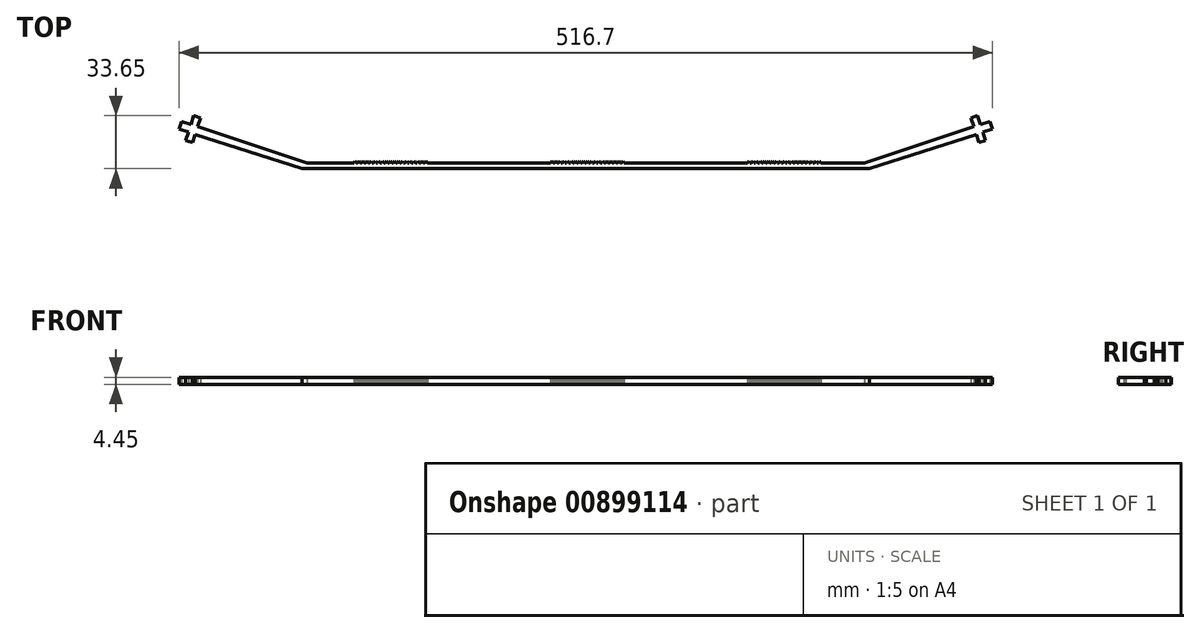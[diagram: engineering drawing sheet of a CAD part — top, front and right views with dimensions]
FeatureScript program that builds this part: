
annotation { "Feature Type Name" : "Feature", "Feature Type Description" : "" }
export const myFeature = defineFeature(function(context is Context, id is Id, definition is map)
    precondition{}
    {
        {
            var Q0;
            Q0=qCreatedBy(makeId("Top.planeOp"),FACE);
            var sketch = newSketch(context, id + "F0", { "sketchPlane" : qUnion([Q0])});
            skLineSegment(sketch, "E0", {"start": v(-260.7, 10.38) * mm, "end": v(94.9, 10.38) * mm});
            skLineSegment(sketch, "E1", {"start": v(-259.95, 14.04) * mm, "end": v(-232.45, 14.04) * mm});
            skLineSegment(sketch, "E2", {"start": v(-84.08, 15.18) * mm, "end": v(-83.22, 14.04) * mm});
            skLineSegment(sketch, "E3.MirrorCS", {"start": v(-84.08, 15.18) * mm, "end": v(-84.95, 14.04) * mm});
            skLineSegment(sketch, "E4.trimOffspring", {"start": v(-83.22, 14.04) * mm, "end": v(-82.45, 14.04) * mm});
            skPoint(sketch, "E5.start.orphan", {"position": v(-84.08, 8) * mm});
            skLineSegment(sketch, "E6.direction1", {"start": v(-83.22, 14.04) * mm, "end": v(-82.45, 14.04) * mm, "construction": true});
            skLineSegment(sketch, "E7.1.0.0", {"start": v(-81.58, 15.18) * mm, "end": v(-80.72, 14.04) * mm});
            skLineSegment(sketch, "E7.1.0.1", {"start": v(-81.58, 15.18) * mm, "end": v(-82.45, 14.04) * mm});
            skLineSegment(sketch, "E7.2.0.0", {"start": v(-79.08, 15.18) * mm, "end": v(-78.22, 14.04) * mm});
            skLineSegment(sketch, "E7.2.0.1", {"start": v(-79.08, 15.18) * mm, "end": v(-79.95, 14.04) * mm});
            skLineSegment(sketch, "E7.3.0.0", {"start": v(-76.58, 15.18) * mm, "end": v(-75.72, 14.04) * mm});
            skLineSegment(sketch, "E7.3.0.1", {"start": v(-76.58, 15.18) * mm, "end": v(-77.45, 14.04) * mm});
            skLineSegment(sketch, "E7.4.0.0", {"start": v(-74.08, 15.18) * mm, "end": v(-73.22, 14.04) * mm});
            skLineSegment(sketch, "E7.4.0.1", {"start": v(-74.08, 15.18) * mm, "end": v(-74.95, 14.04) * mm});
            skLineSegment(sketch, "E7.5.0.0", {"start": v(-71.58, 15.18) * mm, "end": v(-70.72, 14.04) * mm});
            skLineSegment(sketch, "E7.5.0.1", {"start": v(-71.58, 15.18) * mm, "end": v(-72.45, 14.04) * mm});
            skLineSegment(sketch, "E7.6.0.0", {"start": v(-69.08, 15.18) * mm, "end": v(-68.22, 14.04) * mm});
            skLineSegment(sketch, "E7.6.0.1", {"start": v(-69.08, 15.18) * mm, "end": v(-69.95, 14.04) * mm});
            skLineSegment(sketch, "E7.7.0.0", {"start": v(-66.58, 15.18) * mm, "end": v(-65.72, 14.04) * mm});
            skLineSegment(sketch, "E7.7.0.1", {"start": v(-66.58, 15.18) * mm, "end": v(-67.45, 14.04) * mm});
            skLineSegment(sketch, "E7.8.0.0", {"start": v(-64.08, 15.18) * mm, "end": v(-63.22, 14.04) * mm});
            skLineSegment(sketch, "E7.8.0.1", {"start": v(-64.08, 15.18) * mm, "end": v(-64.95, 14.04) * mm});
            skLineSegment(sketch, "E7.9.0.0", {"start": v(-61.58, 15.18) * mm, "end": v(-60.72, 14.04) * mm});
            skLineSegment(sketch, "E7.9.0.1", {"start": v(-61.58, 15.18) * mm, "end": v(-62.45, 14.04) * mm});
            skLineSegment(sketch, "E8.1.0.0", {"start": v(-86.58, 15.18) * mm, "end": v(-87.45, 14.04) * mm});
            skLineSegment(sketch, "E8.1.0.1", {"start": v(-86.58, 15.18) * mm, "end": v(-85.72, 14.04) * mm});
            skLineSegment(sketch, "E8.2.0.0", {"start": v(-89.08, 15.18) * mm, "end": v(-89.95, 14.04) * mm});
            skLineSegment(sketch, "E8.2.0.1", {"start": v(-89.08, 15.18) * mm, "end": v(-88.22, 14.04) * mm});
            skLineSegment(sketch, "E8.3.0.0", {"start": v(-91.58, 15.18) * mm, "end": v(-92.45, 14.04) * mm});
            skLineSegment(sketch, "E8.3.0.1", {"start": v(-91.58, 15.18) * mm, "end": v(-90.72, 14.04) * mm});
            skLineSegment(sketch, "E8.4.0.0", {"start": v(-94.08, 15.18) * mm, "end": v(-94.95, 14.04) * mm});
            skLineSegment(sketch, "E8.4.0.1", {"start": v(-94.08, 15.18) * mm, "end": v(-93.22, 14.04) * mm});
            skLineSegment(sketch, "E8.5.0.0", {"start": v(-96.58, 15.18) * mm, "end": v(-97.45, 14.04) * mm});
            skLineSegment(sketch, "E8.5.0.1", {"start": v(-96.58, 15.18) * mm, "end": v(-95.72, 14.04) * mm});
            skLineSegment(sketch, "E8.6.0.0", {"start": v(-99.08, 15.18) * mm, "end": v(-99.95, 14.04) * mm});
            skLineSegment(sketch, "E8.6.0.1", {"start": v(-99.08, 15.18) * mm, "end": v(-98.22, 14.04) * mm});
            skLineSegment(sketch, "E8.7.0.0", {"start": v(-101.58, 15.18) * mm, "end": v(-102.45, 14.04) * mm});
            skLineSegment(sketch, "E8.7.0.1", {"start": v(-101.58, 15.18) * mm, "end": v(-100.72, 14.04) * mm});
            skLineSegment(sketch, "E8.8.0.0", {"start": v(-104.08, 15.18) * mm, "end": v(-104.95, 14.04) * mm});
            skLineSegment(sketch, "E8.8.0.1", {"start": v(-104.08, 15.18) * mm, "end": v(-103.22, 14.04) * mm});
            skLineSegment(sketch, "E8.9.0.0", {"start": v(-106.58, 15.18) * mm, "end": v(-107.45, 14.04) * mm});
            skLineSegment(sketch, "E8.9.0.1", {"start": v(-106.58, 15.18) * mm, "end": v(-105.72, 14.04) * mm});
            skLineSegment(sketch, "E8.direction1", {"start": v(-84.95, 14.04) * mm, "end": v(-85.72, 14.04) * mm, "construction": true});
            skLineSegment(sketch, "E9.trimOffspring", {"start": v(-105.72, 14.04) * mm, "end": v(-104.95, 14.04) * mm});
            skLineSegment(sketch, "E10.trimOffspring", {"start": v(-103.22, 14.04) * mm, "end": v(-102.45, 14.04) * mm});
            skLineSegment(sketch, "E11.trimOffspring", {"start": v(-100.72, 14.04) * mm, "end": v(-99.95, 14.04) * mm});
            skLineSegment(sketch, "E12.trimOffspring", {"start": v(-95.72, 14.04) * mm, "end": v(-94.95, 14.04) * mm});
            skLineSegment(sketch, "E13.trimOffspring", {"start": v(-98.22, 14.04) * mm, "end": v(-97.45, 14.04) * mm});
            skLineSegment(sketch, "E14.trimOffspring", {"start": v(-93.22, 14.04) * mm, "end": v(-92.45, 14.04) * mm});
            skLineSegment(sketch, "E15.trimOffspring", {"start": v(-90.72, 14.04) * mm, "end": v(-89.95, 14.04) * mm});
            skLineSegment(sketch, "E16.trimOffspring", {"start": v(-88.22, 14.04) * mm, "end": v(-87.45, 14.04) * mm});
            skLineSegment(sketch, "E17.trimOffspring", {"start": v(-85.72, 14.04) * mm, "end": v(-84.95, 14.04) * mm});
            skLineSegment(sketch, "E18.trimOffspring", {"start": v(-80.72, 14.04) * mm, "end": v(-79.95, 14.04) * mm, "construction": true});
            skLineSegment(sketch, "E19.trimOffspring", {"start": v(-80.72, 14.04) * mm, "end": v(-79.95, 14.04) * mm});
            skLineSegment(sketch, "E20.trimOffspring", {"start": v(-78.22, 14.04) * mm, "end": v(-77.45, 14.04) * mm, "construction": true});
            skLineSegment(sketch, "E21.trimOffspring", {"start": v(-78.22, 14.04) * mm, "end": v(-77.45, 14.04) * mm});
            skLineSegment(sketch, "E22.trimOffspring", {"start": v(-75.72, 14.04) * mm, "end": v(-74.95, 14.04) * mm, "construction": true});
            skLineSegment(sketch, "E23.trimOffspring", {"start": v(-73.22, 14.04) * mm, "end": v(-72.45, 14.04) * mm, "construction": true});
            skLineSegment(sketch, "E24.trimOffspring", {"start": v(-73.22, 14.04) * mm, "end": v(-72.45, 14.04) * mm});
            skLineSegment(sketch, "E25", {"start": v(-75.72, 14.04) * mm, "end": v(-74.95, 14.04) * mm});
            skLineSegment(sketch, "E26.trimOffspring", {"start": v(-70.72, 14.04) * mm, "end": v(-69.95, 14.04) * mm, "construction": true});
            skLineSegment(sketch, "E27.trimOffspring", {"start": v(-70.72, 14.04) * mm, "end": v(-69.95, 14.04) * mm});
            skLineSegment(sketch, "E28.trimOffspring", {"start": v(-68.22, 14.04) * mm, "end": v(-67.45, 14.04) * mm, "construction": true});
            skLineSegment(sketch, "E29.trimOffspring", {"start": v(-68.22, 14.04) * mm, "end": v(-67.45, 14.04) * mm});
            skLineSegment(sketch, "E30.trimOffspring", {"start": v(-65.72, 14.04) * mm, "end": v(-64.95, 14.04) * mm, "construction": true});
            skLineSegment(sketch, "E31.trimOffspring", {"start": v(-65.72, 14.04) * mm, "end": v(-64.95, 14.04) * mm});
            skLineSegment(sketch, "E32.trimOffspring", {"start": v(-63.22, 14.04) * mm, "end": v(-62.45, 14.04) * mm, "construction": true});
            skLineSegment(sketch, "E33.trimOffspring", {"start": v(-63.22, 14.04) * mm, "end": v(-62.45, 14.04) * mm});
            skLineSegment(sketch, "E34.trimOffspring", {"start": v(-60.72, 14.04) * mm, "end": v(-58.22, 14.04) * mm, "construction": true});
            skLineSegment(sketch, "E35.trimOffspring", {"start": v(-60.72, 14.04) * mm, "end": v(17.55, 14.04) * mm});
            skLineSegment(sketch, "E36.1.0.0", {"start": v(63.42, 15.18) * mm, "end": v(64.28, 14.04) * mm});
            skLineSegment(sketch, "E36.1.0.1", {"start": v(63.42, 15.18) * mm, "end": v(62.55, 14.04) * mm});
            skLineSegment(sketch, "E36.1.0.2", {"start": v(60.92, 15.18) * mm, "end": v(61.78, 14.04) * mm});
            skLineSegment(sketch, "E36.1.0.3", {"start": v(60.92, 15.18) * mm, "end": v(60.05, 14.04) * mm});
            skLineSegment(sketch, "E36.1.0.4", {"start": v(58.42, 15.18) * mm, "end": v(59.28, 14.04) * mm});
            skLineSegment(sketch, "E36.1.0.5", {"start": v(58.42, 15.18) * mm, "end": v(57.55, 14.04) * mm});
            skLineSegment(sketch, "E36.1.0.6", {"start": v(55.92, 15.18) * mm, "end": v(56.78, 14.04) * mm});
            skLineSegment(sketch, "E36.1.0.7", {"start": v(55.92, 15.18) * mm, "end": v(55.05, 14.04) * mm});
            skLineSegment(sketch, "E36.1.0.8", {"start": v(53.42, 15.18) * mm, "end": v(54.28, 14.04) * mm});
            skLineSegment(sketch, "E36.1.0.9", {"start": v(53.42, 15.18) * mm, "end": v(52.55, 14.04) * mm});
            skLineSegment(sketch, "E36.1.0.10", {"start": v(50.92, 15.18) * mm, "end": v(51.78, 14.04) * mm});
            skLineSegment(sketch, "E36.1.0.11", {"start": v(50.92, 15.18) * mm, "end": v(50.05, 14.04) * mm});
            skLineSegment(sketch, "E36.1.0.12", {"start": v(48.42, 15.18) * mm, "end": v(49.28, 14.04) * mm});
            skLineSegment(sketch, "E36.1.0.13", {"start": v(48.42, 15.18) * mm, "end": v(47.55, 14.04) * mm});
            skLineSegment(sketch, "E36.1.0.14", {"start": v(45.92, 15.18) * mm, "end": v(46.78, 14.04) * mm});
            skLineSegment(sketch, "E36.1.0.15", {"start": v(45.92, 15.18) * mm, "end": v(45.05, 14.04) * mm});
            skLineSegment(sketch, "E36.1.0.16", {"start": v(43.42, 15.18) * mm, "end": v(44.28, 14.04) * mm});
            skLineSegment(sketch, "E36.1.0.17", {"start": v(43.42, 15.18) * mm, "end": v(42.55, 14.04) * mm});
            skLineSegment(sketch, "E36.1.0.18", {"start": v(40.92, 15.18) * mm, "end": v(41.78, 14.04) * mm});
            skLineSegment(sketch, "E36.1.0.19", {"start": v(40.92, 15.18) * mm, "end": v(40.05, 14.04) * mm});
            skLineSegment(sketch, "E36.1.0.20", {"start": v(38.42, 15.18) * mm, "end": v(39.28, 14.04) * mm});
            skLineSegment(sketch, "E36.1.0.21", {"start": v(38.42, 15.18) * mm, "end": v(37.55, 14.04) * mm});
            skLineSegment(sketch, "E36.1.0.22", {"start": v(35.92, 15.18) * mm, "end": v(36.78, 14.04) * mm});
            skLineSegment(sketch, "E36.1.0.23", {"start": v(35.92, 15.18) * mm, "end": v(35.05, 14.04) * mm});
            skLineSegment(sketch, "E36.1.0.24", {"start": v(33.42, 15.18) * mm, "end": v(34.28, 14.04) * mm});
            skLineSegment(sketch, "E36.1.0.25", {"start": v(33.42, 15.18) * mm, "end": v(32.55, 14.04) * mm});
            skLineSegment(sketch, "E36.1.0.26", {"start": v(30.92, 15.18) * mm, "end": v(31.78, 14.04) * mm});
            skLineSegment(sketch, "E36.1.0.27", {"start": v(30.92, 15.18) * mm, "end": v(30.05, 14.04) * mm});
            skLineSegment(sketch, "E36.1.0.28", {"start": v(28.42, 15.18) * mm, "end": v(29.28, 14.04) * mm});
            skLineSegment(sketch, "E36.1.0.29", {"start": v(28.42, 15.18) * mm, "end": v(27.55, 14.04) * mm});
            skLineSegment(sketch, "E36.1.0.30", {"start": v(25.92, 15.18) * mm, "end": v(26.78, 14.04) * mm});
            skLineSegment(sketch, "E36.1.0.31", {"start": v(25.92, 15.18) * mm, "end": v(25.05, 14.04) * mm});
            skLineSegment(sketch, "E36.1.0.32", {"start": v(23.42, 15.18) * mm, "end": v(24.28, 14.04) * mm});
            skLineSegment(sketch, "E36.1.0.33", {"start": v(23.42, 15.18) * mm, "end": v(22.55, 14.04) * mm});
            skLineSegment(sketch, "E36.1.0.34", {"start": v(20.92, 15.18) * mm, "end": v(21.78, 14.04) * mm});
            skLineSegment(sketch, "E36.1.0.35", {"start": v(20.92, 15.18) * mm, "end": v(20.05, 14.04) * mm});
            skLineSegment(sketch, "E36.1.0.36", {"start": v(18.42, 15.18) * mm, "end": v(19.28, 14.04) * mm});
            skLineSegment(sketch, "E36.1.0.37", {"start": v(18.42, 15.18) * mm, "end": v(17.55, 14.04) * mm});
            skLineSegment(sketch, "E37.1.0.0", {"start": v(-186.58, 15.18) * mm, "end": v(-185.72, 14.04) * mm});
            skLineSegment(sketch, "E37.1.0.1", {"start": v(-186.58, 15.18) * mm, "end": v(-187.45, 14.04) * mm});
            skLineSegment(sketch, "E37.1.0.2", {"start": v(-189.08, 15.18) * mm, "end": v(-188.22, 14.04) * mm});
            skLineSegment(sketch, "E37.1.0.3", {"start": v(-189.08, 15.18) * mm, "end": v(-189.95, 14.04) * mm});
            skLineSegment(sketch, "E37.1.0.4", {"start": v(-191.58, 15.18) * mm, "end": v(-190.72, 14.04) * mm});
            skLineSegment(sketch, "E37.1.0.5", {"start": v(-191.58, 15.18) * mm, "end": v(-192.45, 14.04) * mm});
            skLineSegment(sketch, "E37.1.0.6", {"start": v(-194.08, 15.18) * mm, "end": v(-193.22, 14.04) * mm});
            skLineSegment(sketch, "E37.1.0.7", {"start": v(-194.08, 15.18) * mm, "end": v(-194.95, 14.04) * mm});
            skLineSegment(sketch, "E37.1.0.8", {"start": v(-196.58, 15.18) * mm, "end": v(-195.72, 14.04) * mm});
            skLineSegment(sketch, "E37.1.0.9", {"start": v(-196.58, 15.18) * mm, "end": v(-197.45, 14.04) * mm});
            skLineSegment(sketch, "E37.1.0.10", {"start": v(-199.08, 15.18) * mm, "end": v(-198.22, 14.04) * mm});
            skLineSegment(sketch, "E37.1.0.11", {"start": v(-199.08, 15.18) * mm, "end": v(-199.95, 14.04) * mm});
            skLineSegment(sketch, "E37.1.0.12", {"start": v(-201.58, 15.18) * mm, "end": v(-200.72, 14.04) * mm});
            skLineSegment(sketch, "E37.1.0.13", {"start": v(-201.58, 15.18) * mm, "end": v(-202.45, 14.04) * mm});
            skLineSegment(sketch, "E37.1.0.14", {"start": v(-204.08, 15.18) * mm, "end": v(-203.22, 14.04) * mm});
            skLineSegment(sketch, "E37.1.0.15", {"start": v(-204.08, 15.18) * mm, "end": v(-204.95, 14.04) * mm});
            skLineSegment(sketch, "E37.1.0.16", {"start": v(-206.58, 15.18) * mm, "end": v(-205.72, 14.04) * mm});
            skLineSegment(sketch, "E37.1.0.17", {"start": v(-206.58, 15.18) * mm, "end": v(-207.45, 14.04) * mm});
            skLineSegment(sketch, "E37.1.0.18", {"start": v(-209.08, 15.18) * mm, "end": v(-208.22, 14.04) * mm});
            skLineSegment(sketch, "E37.1.0.19", {"start": v(-209.08, 15.18) * mm, "end": v(-209.95, 14.04) * mm});
            skLineSegment(sketch, "E37.1.0.20", {"start": v(-231.58, 15.18) * mm, "end": v(-232.45, 14.04) * mm});
            skLineSegment(sketch, "E37.1.0.21", {"start": v(-231.58, 15.18) * mm, "end": v(-230.72, 14.04) * mm});
            skLineSegment(sketch, "E37.1.0.22", {"start": v(-229.08, 15.18) * mm, "end": v(-229.95, 14.04) * mm});
            skLineSegment(sketch, "E37.1.0.23", {"start": v(-229.08, 15.18) * mm, "end": v(-228.22, 14.04) * mm});
            skLineSegment(sketch, "E37.1.0.24", {"start": v(-226.58, 15.18) * mm, "end": v(-227.45, 14.04) * mm});
            skLineSegment(sketch, "E37.1.0.25", {"start": v(-226.58, 15.18) * mm, "end": v(-225.72, 14.04) * mm});
            skLineSegment(sketch, "E37.1.0.26", {"start": v(-224.08, 15.18) * mm, "end": v(-224.95, 14.04) * mm});
            skLineSegment(sketch, "E37.1.0.27", {"start": v(-224.08, 15.18) * mm, "end": v(-223.22, 14.04) * mm});
            skLineSegment(sketch, "E37.1.0.28", {"start": v(-221.58, 15.18) * mm, "end": v(-222.45, 14.04) * mm});
            skLineSegment(sketch, "E37.1.0.29", {"start": v(-221.58, 15.18) * mm, "end": v(-220.72, 14.04) * mm});
            skLineSegment(sketch, "E37.1.0.30", {"start": v(-219.08, 15.18) * mm, "end": v(-219.95, 14.04) * mm});
            skLineSegment(sketch, "E37.1.0.31", {"start": v(-219.08, 15.18) * mm, "end": v(-218.22, 14.04) * mm});
            skLineSegment(sketch, "E37.1.0.32", {"start": v(-216.58, 15.18) * mm, "end": v(-217.45, 14.04) * mm});
            skLineSegment(sketch, "E37.1.0.33", {"start": v(-216.58, 15.18) * mm, "end": v(-215.72, 14.04) * mm});
            skLineSegment(sketch, "E37.1.0.34", {"start": v(-214.08, 15.18) * mm, "end": v(-214.95, 14.04) * mm});
            skLineSegment(sketch, "E37.1.0.35", {"start": v(-214.08, 15.18) * mm, "end": v(-213.22, 14.04) * mm});
            skLineSegment(sketch, "E37.1.0.36", {"start": v(-211.58, 15.18) * mm, "end": v(-212.45, 14.04) * mm});
            skLineSegment(sketch, "E37.1.0.37", {"start": v(-211.58, 15.18) * mm, "end": v(-210.72, 14.04) * mm});
            skLineSegment(sketch, "E37.direction1", {"start": v(-60.72, 14.04) * mm, "end": v(-185.72, 14.04) * mm, "construction": true});
            skLineSegment(sketch, "E38.trimOffspring", {"start": v(-230.72, 14.04) * mm, "end": v(-229.95, 14.04) * mm});
            skLineSegment(sketch, "E39.trimOffspring", {"start": v(-228.22, 14.04) * mm, "end": v(-227.45, 14.04) * mm});
            skLineSegment(sketch, "E40.trimOffspring", {"start": v(-225.72, 14.04) * mm, "end": v(-224.95, 14.04) * mm});
            skLineSegment(sketch, "E41.trimOffspring", {"start": v(-223.22, 14.04) * mm, "end": v(-222.45, 14.04) * mm});
            skLineSegment(sketch, "E42.trimOffspring", {"start": v(-220.72, 14.04) * mm, "end": v(-219.95, 14.04) * mm});
            skLineSegment(sketch, "E43.trimOffspring", {"start": v(-218.22, 14.04) * mm, "end": v(-217.45, 14.04) * mm});
            skLineSegment(sketch, "E44.trimOffspring", {"start": v(-215.72, 14.04) * mm, "end": v(-214.95, 14.04) * mm});
            skLineSegment(sketch, "E45.trimOffspring", {"start": v(-213.22, 14.04) * mm, "end": v(-212.45, 14.04) * mm});
            skLineSegment(sketch, "E46.trimOffspring", {"start": v(-210.72, 14.04) * mm, "end": v(-209.95, 14.04) * mm});
            skLineSegment(sketch, "E47.trimOffspring", {"start": v(-208.22, 14.04) * mm, "end": v(-207.45, 14.04) * mm});
            skLineSegment(sketch, "E48.trimOffspring", {"start": v(-205.72, 14.04) * mm, "end": v(-204.95, 14.04) * mm});
            skLineSegment(sketch, "E49.trimOffspring", {"start": v(-203.22, 14.04) * mm, "end": v(-202.45, 14.04) * mm});
            skLineSegment(sketch, "E50.trimOffspring", {"start": v(-200.72, 14.04) * mm, "end": v(-199.95, 14.04) * mm});
            skLineSegment(sketch, "E51.trimOffspring", {"start": v(-198.22, 14.04) * mm, "end": v(-197.45, 14.04) * mm});
            skLineSegment(sketch, "E52.trimOffspring", {"start": v(-195.72, 14.04) * mm, "end": v(-194.95, 14.04) * mm});
            skLineSegment(sketch, "E53.trimOffspring", {"start": v(-193.22, 14.04) * mm, "end": v(-192.45, 14.04) * mm});
            skLineSegment(sketch, "E54.trimOffspring", {"start": v(-190.72, 14.04) * mm, "end": v(-189.95, 14.04) * mm});
            skLineSegment(sketch, "E55.trimOffspring", {"start": v(-188.22, 14.04) * mm, "end": v(-187.45, 14.04) * mm});
            skLineSegment(sketch, "E56.trimOffspring", {"start": v(-185.72, 14.04) * mm, "end": v(-107.45, 14.04) * mm});
            skLineSegment(sketch, "E57.trimOffspring", {"start": v(64.28, 14.04) * mm, "end": v(91.78, 14.04) * mm});
            skLineSegment(sketch, "E58.trimOffspring", {"start": v(61.78, 14.04) * mm, "end": v(62.55, 14.04) * mm, "construction": true});
            skLineSegment(sketch, "E59.trimOffspring", {"start": v(61.78, 14.04) * mm, "end": v(62.55, 14.04) * mm});
            skLineSegment(sketch, "E60.trimOffspring", {"start": v(59.28, 14.04) * mm, "end": v(60.05, 14.04) * mm, "construction": true});
            skLineSegment(sketch, "E61.trimOffspring", {"start": v(59.28, 14.04) * mm, "end": v(60.05, 14.04) * mm});
            skLineSegment(sketch, "E62.trimOffspring", {"start": v(56.78, 14.04) * mm, "end": v(57.55, 14.04) * mm, "construction": true});
            skLineSegment(sketch, "E63.trimOffspring", {"start": v(56.78, 14.04) * mm, "end": v(57.55, 14.04) * mm});
            skLineSegment(sketch, "E64.trimOffspring", {"start": v(54.28, 14.04) * mm, "end": v(55.05, 14.04) * mm, "construction": true});
            skLineSegment(sketch, "E65.trimOffspring", {"start": v(54.28, 14.04) * mm, "end": v(55.05, 14.04) * mm});
            skLineSegment(sketch, "E66.trimOffspring", {"start": v(51.78, 14.04) * mm, "end": v(52.55, 14.04) * mm});
            skLineSegment(sketch, "E67.trimOffspring", {"start": v(49.28, 14.04) * mm, "end": v(50.05, 14.04) * mm});
            skLineSegment(sketch, "E68.trimOffspring", {"start": v(46.78, 14.04) * mm, "end": v(47.55, 14.04) * mm});
            skLineSegment(sketch, "E69.trimOffspring", {"start": v(44.28, 14.04) * mm, "end": v(45.05, 14.04) * mm});
            skLineSegment(sketch, "E70.trimOffspring", {"start": v(41.78, 14.04) * mm, "end": v(42.55, 14.04) * mm});
            skLineSegment(sketch, "E71.trimOffspring", {"start": v(39.28, 14.04) * mm, "end": v(40.05, 14.04) * mm});
            skLineSegment(sketch, "E72.trimOffspring", {"start": v(36.78, 14.04) * mm, "end": v(37.55, 14.04) * mm});
            skLineSegment(sketch, "E73.trimOffspring", {"start": v(34.28, 14.04) * mm, "end": v(35.05, 14.04) * mm});
            skLineSegment(sketch, "E74.trimOffspring", {"start": v(19.28, 14.04) * mm, "end": v(20.05, 14.04) * mm});
            skLineSegment(sketch, "E75.trimOffspring", {"start": v(21.78, 14.04) * mm, "end": v(22.55, 14.04) * mm});
            skLineSegment(sketch, "E76.trimOffspring", {"start": v(24.28, 14.04) * mm, "end": v(25.05, 14.04) * mm});
            skLineSegment(sketch, "E77.trimOffspring", {"start": v(26.78, 14.04) * mm, "end": v(27.55, 14.04) * mm});
            skLineSegment(sketch, "E78.trimOffspring", {"start": v(29.28, 14.04) * mm, "end": v(30.05, 14.04) * mm});
            skLineSegment(sketch, "E79.trimOffspring", {"start": v(31.78, 14.04) * mm, "end": v(32.55, 14.04) * mm});
            skLineSegment(sketch, "E80.MirrorCS", {"start": v(163.72, 44.03) * mm, "end": v(159.49, 42.67) * mm});
            skLineSegment(sketch, "E81.MirrorCS", {"start": v(173.14, 35.48) * mm, "end": v(171.55, 40.42) * mm});
            skLineSegment(sketch, "E82.MirrorCS", {"start": v(164.58, 26.83) * mm, "end": v(168.82, 28.19) * mm});
            skLineSegment(sketch, "E83.MirrorCS", {"start": v(171.55, 40.42) * mm, "end": v(165.5, 38.48) * mm});
            skLineSegment(sketch, "E84.MirrorCS", {"start": v(168.82, 28.19) * mm, "end": v(167.1, 33.54) * mm});
            skLineSegment(sketch, "E85.MirrorCS", {"start": v(162.87, 32.18) * mm, "end": v(164.58, 26.83) * mm});
            skLineSegment(sketch, "E86.MirrorCS", {"start": v(165.5, 38.48) * mm, "end": v(163.72, 44.03) * mm});
            skLineSegment(sketch, "E87.MirrorCS", {"start": v(169.27, 34.24) * mm, "end": v(173.14, 35.48) * mm});
            skLineSegment(sketch, "E88.MirrorCS", {"start": v(161.27, 37.12) * mm, "end": v(91.78, 14.04) * mm});
            skLineSegment(sketch, "E89.MirrorCS", {"start": v(159.49, 42.67) * mm, "end": v(161.27, 37.12) * mm});
            skLineSegment(sketch, "E90.MirrorCS", {"start": v(94.9, 10.38) * mm, "end": v(162.87, 32.18) * mm});
            skLineSegment(sketch, "E91", {"start": v(169.27, 34.24) * mm, "end": v(167.1, 33.54) * mm});
            skLineSegment(sketch, "E92.MirrorCS", {"start": v(-339.24, 28.19) * mm, "end": v(-337.52, 33.54) * mm});
            skLineSegment(sketch, "E93.MirrorCS", {"start": v(-339.7, 34.24) * mm, "end": v(-337.52, 33.54) * mm});
            skLineSegment(sketch, "E94.MirrorCS", {"start": v(-339.7, 34.24) * mm, "end": v(-343.56, 35.48) * mm});
            skLineSegment(sketch, "E95.MirrorCS", {"start": v(-343.56, 35.48) * mm, "end": v(-341.97, 40.42) * mm});
            skLineSegment(sketch, "E96.MirrorCS", {"start": v(-333.29, 32.18) * mm, "end": v(-335, 26.83) * mm});
            skLineSegment(sketch, "E97.MirrorCS", {"start": v(-329.9, 42.67) * mm, "end": v(-331.69, 37.12) * mm});
            skLineSegment(sketch, "E98.MirrorCS", {"start": v(-335.93, 38.48) * mm, "end": v(-334.14, 44.03) * mm});
            skLineSegment(sketch, "E99.MirrorCS", {"start": v(-334.14, 44.03) * mm, "end": v(-329.9, 42.67) * mm});
            skLineSegment(sketch, "E100.MirrorCS", {"start": v(-341.97, 40.42) * mm, "end": v(-335.93, 38.48) * mm});
            skLineSegment(sketch, "E101.MirrorCS", {"start": v(-335, 26.83) * mm, "end": v(-339.24, 28.19) * mm});
            skLineSegment(sketch, "E102.MirrorCS", {"start": v(-331.69, 37.12) * mm, "end": v(-262.2, 14.04) * mm});
            skLineSegment(sketch, "E103.MirrorCS", {"start": v(-265.31, 10.38) * mm, "end": v(-333.29, 32.18) * mm});
            skLineSegment(sketch, "E104", {"start": v(-260.7, 10.38) * mm, "end": v(-262.72, 10.38) * mm});
            skLineSegment(sketch, "E105", {"start": v(-267.03, 10.38) * mm, "end": v(-262.72, 10.38) * mm});
            skLineSegment(sketch, "E106", {"start": v(-259.95, 14.04) * mm, "end": v(-263.91, 14.04) * mm});
            skSolve(sketch);
        }
        {
            var Q0;
            Q0=makeQuery(id+"F0.imprint","IMPRINT",FACE,{"disambiguationData":[TD([[makeQuery(id+"F0.imprint","IMPRINT",EDGE,{"derivedFrom":sQuery(id+"F0.wireOp",EDGE,"E0")}),1.0]])]});
            extrude(context, id + "F1", {"entities" : qUnion([Q0]), "depth" : 4.45 * mm, "offsetDistance" : 25 * mm});
        }
    });
